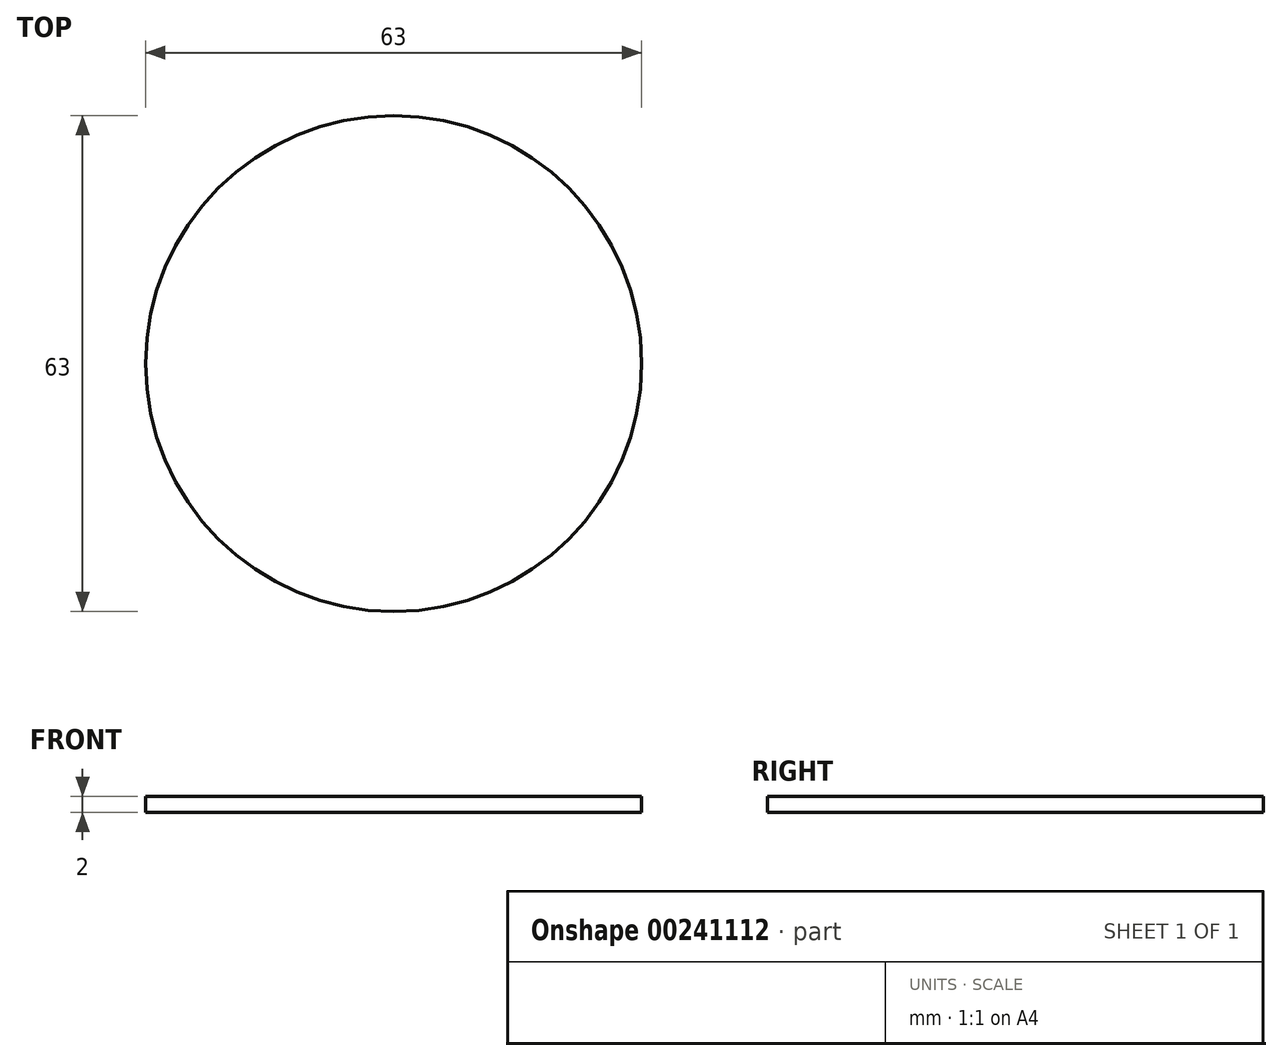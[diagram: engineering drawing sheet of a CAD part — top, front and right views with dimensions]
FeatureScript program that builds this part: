
annotation { "Feature Type Name" : "Feature", "Feature Type Description" : "" }
export const myFeature = defineFeature(function(context is Context, id is Id, definition is map)
    precondition{}
    {
        {
            var Q0;
            Q0=qCreatedBy(makeId("Top.planeOp"),FACE);
            var sketch = newSketch(context, id + "F0", { "sketchPlane" : qUnion([Q0])});
            skCircle(sketch, "E0", {"center": v(0, 0) * mm, "radius": 31.5 * mm});
            skSolve(sketch);
        }
        {
            var Q0;
            Q0=qSketchRegion(id+"F0",true);
            extrude(context, id + "F1", {"entities" : qUnion([Q0]), "depth" : 2 * mm});
        }
    });
